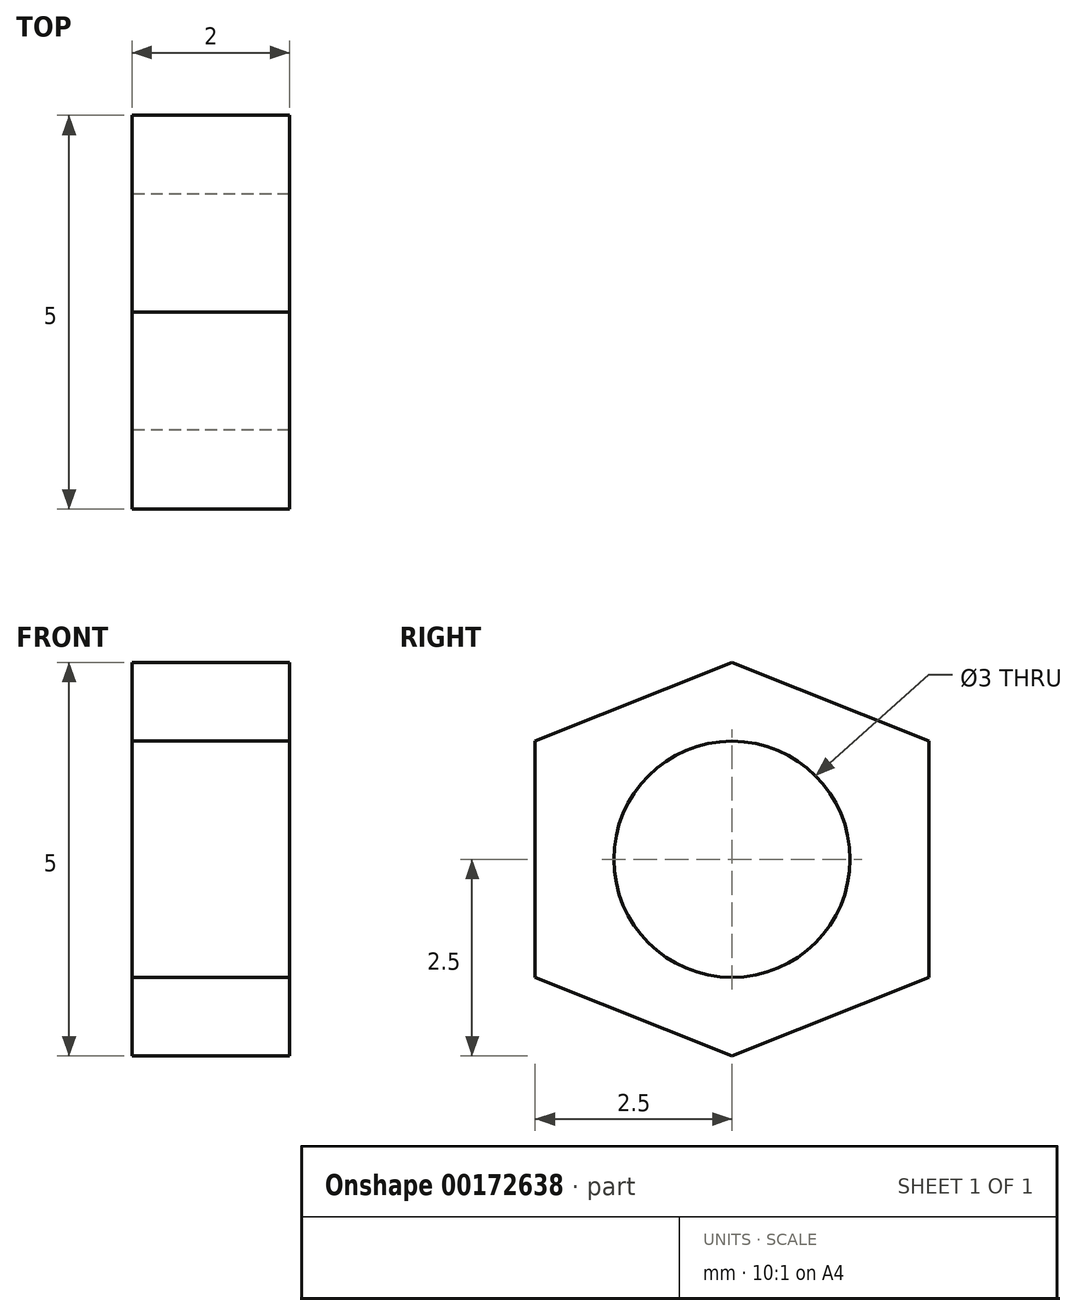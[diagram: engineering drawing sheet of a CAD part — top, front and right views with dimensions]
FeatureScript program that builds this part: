
annotation { "Feature Type Name" : "Feature", "Feature Type Description" : "" }
export const myFeature = defineFeature(function(context is Context, id is Id, definition is map)
    precondition{}
    {
        {
            var Q0;
            Q0=qCreatedBy(makeId("Top.planeOp"),FACE);
            var sketch = newSketch(context, id + "F0", { "sketchPlane" : qUnion([Q0])});
            skCircle(sketch, "E0", {"center": v(0, 0) * mm, "radius": 1.5 * mm});
            skLineSegment(sketch, "E1.bottom", {"start": v(-1.5, 2.5) * mm, "end": v(1.5, 2.5) * mm});
            skLineSegment(sketch, "E1.top", {"start": v(-1.5, -2.5) * mm, "end": v(1.5, -2.5) * mm});
            skPoint(sketch, "E2", {"position": v(-2.5, 0) * mm});
            skPoint(sketch, "E3", {"position": v(2.5, 0) * mm});
            skLineSegment(sketch, "E4", {"start": v(-2.5, 0) * mm, "end": v(-1.5, 2.5) * mm});
            skLineSegment(sketch, "E5", {"start": v(-2.5, 0) * mm, "end": v(-1.5, -2.5) * mm});
            skLineSegment(sketch, "E6", {"start": v(1.5, -2.5) * mm, "end": v(2.5, 0) * mm});
            skLineSegment(sketch, "E7", {"start": v(2.5, 0) * mm, "end": v(1.5, 2.5) * mm});
            skSolve(sketch);
        }
        {
            var Q0;
            Q0=qSketchRegion(id+"F0",true);
            extrude(context, id + "F1", {"entities" : qUnion([Q0]), "depth" : 2 * mm});
        }
        {
            var Q0;
            Q0=qCreatedBy(makeId("Right.planeOp"),FACE);
            var sketch = newSketch(context, id + "F2", { "sketchPlane" : qUnion([Q0])});
            skLineSegment(sketch, "E8", {"start": v(-19.64, 0) * mm, "end": v(19.04, 0) * mm, "construction": true});
            skSolve(sketch);
        }
        {
            var Q0;
            Q0=makeQuery(id+"F1.opExtrude","SWEPT_BODY",BODY,{"disambiguationData":[OSD([sQuery(id+"F0.wireOp",EDGE,"E0"),sQuery(id+"F0.wireOp",EDGE,"E1.bottom"),sQuery(id+"F0.wireOp",EDGE,"E1.top"),sQuery(id+"F0.wireOp",EDGE,"E4"),sQuery(id+"F0.wireOp",EDGE,"E5"),sQuery(id+"F0.wireOp",EDGE,"E6"),sQuery(id+"F0.wireOp",EDGE,"E7")])]});
            var Q1;
            Q1=sQuery(id+"F2.wireOp",EDGE,"E8");
            transform(context, id + "F3", {"entities" : qUnion([Q0]), "transformType" : TransformType.ROTATION, "transformAxis" : qUnion([Q1]), "angle" : 90 * degree, "makeCopy" : false});
        }
    });
